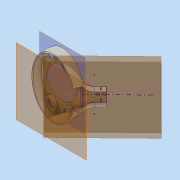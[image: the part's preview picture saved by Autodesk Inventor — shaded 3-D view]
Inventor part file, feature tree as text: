
AUTODESK INVENTOR PART (.ipt)
format: ipt  version: 2019 (Build 230136000, 136)  size: 466,944 bytes
history: native  units: mm
features: other x16, extrude x4, sketch x3, chamfer x1, shell x1, loft x1
ambient origin geometry x8: Origin, YZ Plane, XZ Plane, XY Plane, X Axis, Y Axis, Z Axis, Center Point
bodies: Body1 (feature_tree), Body2 (feature_tree), Body3 (feature_tree)
feature tree (26):
  other  "Твердое тело1"
  other  "Основной эскиз"
  extrude  "Выдавливание1"  Depth=34.31mm
  sketch  "Эскиз7"
  extrude  "Эллипс"  Depth=8.0mm
  other  "РабПлоскость18"
  sketch  "Эскиз19"
  extrude  "Дырки"  Depth=34.31mm
  chamfer  "Фаска для дырок"  Distance=8.0mm
  shell  "Оболочка12"  Thickness=17.93mm
  other  "РабПлоскость33"
  other  "РабПлоскость34"
  sketch  "Эскиз26"
  extrude  "Выдавливание23"  Depth=25.93mm
  loft  "Лофт7"
  other  "Удаление грани5"
  other  "Удаление грани6"
  other  "Удаление грани7"
  other  "Удаление грани8"
  other  "Удаление грани9"
  other  "Удаление грани10"
  other  "Удаление грани11"
  other  "Твердое тело7"
  other  "Твердое тело13"
  other  "Ребра12"
  other  "Ребра13"
